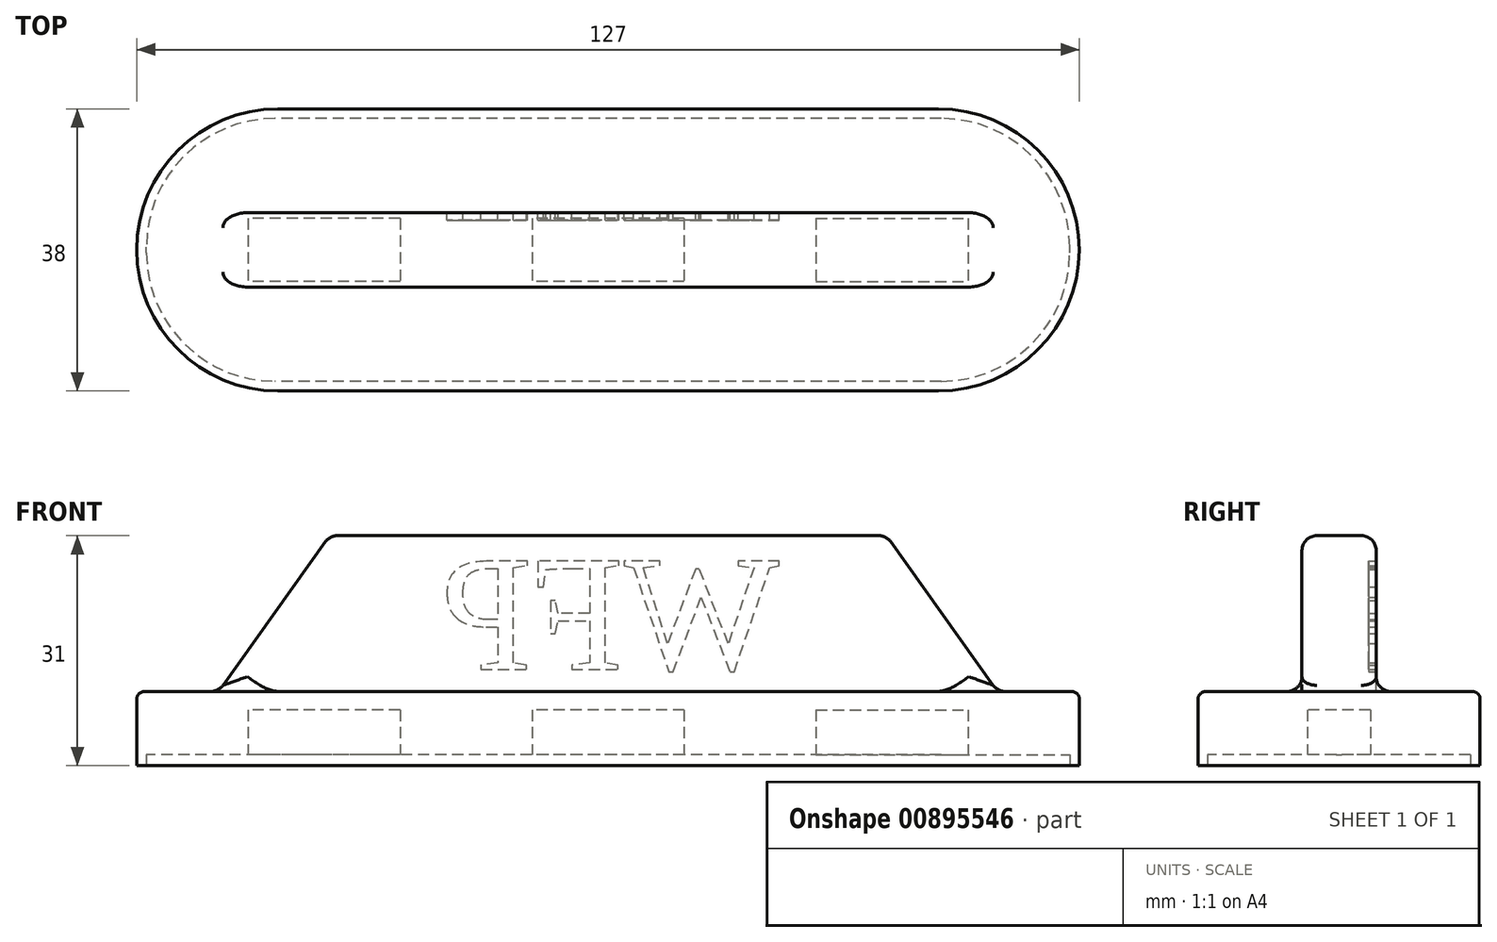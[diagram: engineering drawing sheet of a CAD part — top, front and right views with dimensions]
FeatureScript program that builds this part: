
annotation { "Feature Type Name" : "Feature", "Feature Type Description" : "" }
export const myFeature = defineFeature(function(context is Context, id is Id, definition is map)
    precondition{}
    {
        {
            var Q0;
            Q0=qCreatedBy(makeId("Top.planeOp"),FACE);
            var sketch = newSketch(context, id + "F0", { "sketchPlane" : qUnion([Q0])});
            skLineSegment(sketch, "E0.bottom", {"start": v(44.5, 19) * mm, "end": v(-44.5, 19) * mm});
            skLineSegment(sketch, "E0.top", {"start": v(44.5, -19) * mm, "end": v(-44.5, -19) * mm});
            skLineSegment(sketch, "E0.left", {"start": v(63.5, 0) * mm, "end": v(63.5, 0) * mm});
            skLineSegment(sketch, "E0.right", {"start": v(-63.5, 0) * mm, "end": v(-63.5, 0) * mm});
            skPoint(sketch, "E0.middle", {"position": v(0, 0) * mm});
            skPoint(sketch, "E1.visualSharp", {"position": v(-63.5, 19) * mm});
            skArc(sketch, "E1.filletArc", {"start": v(-44.5, 19) * mm, "mid": v(-57.94, 13.44) * mm, "end": v(-63.5, 0) * mm});
            skPoint(sketch, "E2.visualSharp", {"position": v(-63.5, -19) * mm});
            skArc(sketch, "E2.filletArc", {"start": v(-63.5, 0) * mm, "mid": v(-57.94, -13.44) * mm, "end": v(-44.5, -19) * mm});
            skPoint(sketch, "E3.visualSharp", {"position": v(63.5, 19) * mm});
            skArc(sketch, "E3.filletArc", {"start": v(63.5, 0) * mm, "mid": v(57.94, 13.44) * mm, "end": v(44.5, 19) * mm});
            skPoint(sketch, "E4.visualSharp", {"position": v(63.5, -19) * mm});
            skArc(sketch, "E4.filletArc", {"start": v(44.5, -19) * mm, "mid": v(57.94, -13.44) * mm, "end": v(63.5, 0) * mm});
            skSolve(sketch);
        }
        {
            var Q0;
            Q0=qSketchRegion(id+"F0",true);
            extrude(context, id + "F1", {"entities" : qUnion([Q0]), "depth" : 10 * mm, "offsetDistance" : 25 * mm});
        }
        {
            var Q0;
            Q0=makeQuery(id+"F1.opExtrude","CAP_FACE",FACE,{"disambiguationData":[OSD([sQuery(id+"F0.wireOp",EDGE,"E0.bottom"),sQuery(id+"F0.wireOp",EDGE,"E0.top"),sQuery(id+"F0.wireOp",EDGE,"E1.filletArc"),sQuery(id+"F0.wireOp",EDGE,"E2.filletArc"),sQuery(id+"F0.wireOp",EDGE,"E3.filletArc"),sQuery(id+"F0.wireOp",EDGE,"E4.filletArc")])],"isStart":false});
            var sketch = newSketch(context, id + "F2", { "sketchPlane" : qUnion([Q0])});
            skLineSegment(sketch, "E5.bottom", {"start": v(52.5, 5) * mm, "end": v(-52.5, 5) * mm});
            skLineSegment(sketch, "E5.top", {"start": v(52.5, -5) * mm, "end": v(-52.5, -5) * mm});
            skLineSegment(sketch, "E5.left", {"start": v(52.5, 5) * mm, "end": v(52.5, -5) * mm});
            skLineSegment(sketch, "E5.right", {"start": v(-52.5, 5) * mm, "end": v(-52.5, -5) * mm});
            skPoint(sketch, "E5.middle", {"position": v(0, 0) * mm});
            skSolve(sketch);
        }
        {
            var Q0;
            Q0=qSketchRegion(id+"F2",true);
            extrude(context, id + "F3", {"entities" : qUnion([Q0]), "operationType" : NewBodyOperationType.ADD, "depth" : 21 * mm, "offsetDistance" : 25 * mm});
        }
        {
            var Q0;
            Q0=makeQuery(id+"F3.opExtrude","SWEPT_FACE",FACE,{"disambiguationData":[OSD([sQuery(id+"F2.wireOp",EDGE,"E5.top")])]});
            var sketch = newSketch(context, id + "F4", { "sketchPlane" : qUnion([Q0])});
            skLineSegment(sketch, "E6", {"start": v(-52.5, 10) * mm, "end": v(-37.5, 31) * mm});
            skLineSegment(sketch, "E7", {"start": v(-37.5, 31) * mm, "end": v(-52.5, 31) * mm});
            skLineSegment(sketch, "E8", {"start": v(-52.5, 31) * mm, "end": v(-52.5, 10) * mm});
            skLineSegment(sketch, "E9", {"start": v(52.5, 10) * mm, "end": v(37.5, 31) * mm});
            skLineSegment(sketch, "E10", {"start": v(37.5, 31) * mm, "end": v(52.5, 31) * mm});
            skLineSegment(sketch, "E11", {"start": v(52.5, 31) * mm, "end": v(52.5, 10) * mm});
            skSolve(sketch);
        }
        {
            var Q0;
            Q0=makeQuery(id+"F4.imprint","IMPRINT",FACE,{"disambiguationData":[TD([[makeQuery(id+"F4.imprint","IMPRINT",EDGE,{"derivedFrom":sQuery(id+"F4.wireOp",EDGE,"E6")}),1.0]])]});
            var Q1;
            Q1=makeQuery(id+"F4.imprint","IMPRINT",FACE,{"disambiguationData":[TD([[makeQuery(id+"F4.imprint","IMPRINT",EDGE,{"derivedFrom":sQuery(id+"F4.wireOp",EDGE,"E9")}),-1.0]])]});
            extrude(context, id + "F5", {"entities" : qUnion([Q0, Q1]), "operationType" : NewBodyOperationType.REMOVE, "oppositeDirection" : true, "depth" : 10 * mm, "offsetDistance" : 25 * mm});
        }
        {
            var Q0;
            Q0=makeQuery(id+"F5.boolean.opBoolean","COPY",FACE,{"derivedFrom":makeQuery(id+"F5.opExtrude","SWEPT_FACE",FACE,{"disambiguationData":[OSD([sQuery(id+"F4.wireOp",EDGE,"E6")])]})});
            var Q1;
            Q1=makeQuery(id+"F3.opExtrude","CAP_FACE",FACE,{"disambiguationData":[OSD([sQuery(id+"F2.wireOp",EDGE,"E5.bottom"),sQuery(id+"F2.wireOp",EDGE,"E5.top"),sQuery(id+"F2.wireOp",EDGE,"E5.left"),sQuery(id+"F2.wireOp",EDGE,"E5.right")])],"isStart":false});
            var Q2;
            Q2=makeQuery(id+"F5.boolean.opBoolean","COPY",FACE,{"derivedFrom":makeQuery(id+"F5.opExtrude","SWEPT_FACE",FACE,{"disambiguationData":[OSD([sQuery(id+"F4.wireOp",EDGE,"E9")])]})});
            fillet(context, id + "F6", {"entities" : qUnion([Q0, Q1, Q2]), "radius" : 2 * mm, "tangentPropagation" : true, "allowEdgeOverflow" : false});
        }
        {
            var Q0;
            Q0=makeQuery(id+"F1.opExtrude","CAP_FACE",FACE,{"disambiguationData":[OSD([sQuery(id+"F0.wireOp",EDGE,"E0.bottom"),sQuery(id+"F0.wireOp",EDGE,"E0.top"),sQuery(id+"F0.wireOp",EDGE,"E1.filletArc"),sQuery(id+"F0.wireOp",EDGE,"E2.filletArc"),sQuery(id+"F0.wireOp",EDGE,"E3.filletArc"),sQuery(id+"F0.wireOp",EDGE,"E4.filletArc")])],"isStart":true});
            var sketch = newSketch(context, id + "F7", { "sketchPlane" : qUnion([Q0])});
            skPoint(sketch, "E12.middle", {"position": v(0, 0) * mm});
            skLineSegment(sketch, "E13.bottom", {"start": v(44.9, 17.7) * mm, "end": v(-44.9, 17.7) * mm});
            skLineSegment(sketch, "E13.top", {"start": v(44.9, -17.7) * mm, "end": v(-44.9, -17.7) * mm});
            skLineSegment(sketch, "E13.left", {"start": v(62.2, 0.4) * mm, "end": v(62.2, -0.4) * mm});
            skLineSegment(sketch, "E13.right", {"start": v(-62.2, 0.4) * mm, "end": v(-62.2, -0.4) * mm});
            skPoint(sketch, "E14.visualSharp", {"position": v(62.2, 17.7) * mm});
            skArc(sketch, "E14.filletArc", {"start": v(62.2, 0.4) * mm, "mid": v(57.13, 12.63) * mm, "end": v(44.9, 17.7) * mm});
            skPoint(sketch, "E15.visualSharp", {"position": v(62.2, -17.7) * mm});
            skArc(sketch, "E15.filletArc", {"start": v(44.9, -17.7) * mm, "mid": v(57.13, -12.63) * mm, "end": v(62.2, -0.4) * mm});
            skPoint(sketch, "E16.visualSharp", {"position": v(-62.2, -17.7) * mm});
            skArc(sketch, "E16.filletArc", {"start": v(-62.2, -0.4) * mm, "mid": v(-57.13, -12.63) * mm, "end": v(-44.9, -17.7) * mm});
            skPoint(sketch, "E17.visualSharp", {"position": v(-62.2, 17.7) * mm});
            skArc(sketch, "E17.filletArc", {"start": v(-44.9, 17.7) * mm, "mid": v(-57.13, 12.63) * mm, "end": v(-62.2, 0.4) * mm});
            skSolve(sketch);
        }
        {
            var Q0;
            Q0=makeQuery(id+"F7.imprint","IMPRINT",FACE,{"disambiguationData":[TD([[makeQuery(id+"F7.imprint","IMPRINT",EDGE,{"derivedFrom":sQuery(id+"F7.wireOp",EDGE,"E13.bottom")}),1.0]])]});
            extrude(context, id + "F8", {"entities" : qUnion([Q0]), "operationType" : NewBodyOperationType.REMOVE, "oppositeDirection" : true, "depth" : 1.5 * mm, "offsetDistance" : 25 * mm});
        }
        {
            var Q0;
            Q0=makeQuery(id+"F8.boolean.opBoolean","COPY",FACE,{"derivedFrom":makeQuery(id+"F8.opExtrude","CAP_FACE",FACE,{"disambiguationData":[OSD([sQuery(id+"F7.wireOp",EDGE,"E13.bottom"),sQuery(id+"F7.wireOp",EDGE,"E13.top"),sQuery(id+"F7.wireOp",EDGE,"E13.left"),sQuery(id+"F7.wireOp",EDGE,"E13.right"),sQuery(id+"F7.wireOp",EDGE,"E14.filletArc"),sQuery(id+"F7.wireOp",EDGE,"E15.filletArc"),sQuery(id+"F7.wireOp",EDGE,"E16.filletArc"),sQuery(id+"F7.wireOp",EDGE,"E17.filletArc")])],"isStart":false})});
            var sketch = newSketch(context, id + "F9", { "sketchPlane" : qUnion([Q0])});
            skLineSegment(sketch, "E18.bottom", {"start": v(10.25, -4.25) * mm, "end": v(-10.25, -4.25) * mm});
            skLineSegment(sketch, "E18.top", {"start": v(10.25, 4.25) * mm, "end": v(-10.25, 4.25) * mm});
            skLineSegment(sketch, "E18.left", {"start": v(10.25, -4.25) * mm, "end": v(10.25, 4.25) * mm});
            skLineSegment(sketch, "E18.right", {"start": v(-10.25, -4.25) * mm, "end": v(-10.25, 4.25) * mm});
            skPoint(sketch, "E18.middle", {"position": v(0, 0) * mm});
            skLineSegment(sketch, "E19.bottom", {"start": v(28, -4.25) * mm, "end": v(48.5, -4.25) * mm});
            skLineSegment(sketch, "E19.top", {"start": v(28, 4.25) * mm, "end": v(48.5, 4.25) * mm});
            skLineSegment(sketch, "E19.left", {"start": v(28, -4.25) * mm, "end": v(28, 4.25) * mm});
            skLineSegment(sketch, "E19.right", {"start": v(48.5, -4.25) * mm, "end": v(48.5, 4.25) * mm});
            skPoint(sketch, "E19.middle", {"position": v(38.25, 0) * mm});
            skLineSegment(sketch, "E20.bottom", {"start": v(-28, -4.25) * mm, "end": v(-48.5, -4.25) * mm});
            skLineSegment(sketch, "E20.top", {"start": v(-28, 4.25) * mm, "end": v(-48.5, 4.25) * mm});
            skLineSegment(sketch, "E20.left", {"start": v(-28, -4.25) * mm, "end": v(-28, 4.25) * mm});
            skLineSegment(sketch, "E20.right", {"start": v(-48.5, -4.25) * mm, "end": v(-48.5, 4.25) * mm});
            skPoint(sketch, "E20.middle", {"position": v(-38.25, 0) * mm});
            skSolve(sketch);
        }
        {
            var Q0;
            Q0=makeQuery(id+"F9.imprint","IMPRINT",FACE,{"disambiguationData":[TD([[makeQuery(id+"F9.imprint","IMPRINT",EDGE,{"derivedFrom":sQuery(id+"F9.wireOp",EDGE,"E19.bottom")}),1.0]])]});
            var Q1;
            Q1=makeQuery(id+"F9.imprint","IMPRINT",FACE,{"disambiguationData":[TD([[makeQuery(id+"F9.imprint","IMPRINT",EDGE,{"derivedFrom":sQuery(id+"F9.wireOp",EDGE,"E18.bottom")}),-1.0]])]});
            var Q2;
            Q2=makeQuery(id+"F9.imprint","IMPRINT",FACE,{"disambiguationData":[TD([[makeQuery(id+"F9.imprint","IMPRINT",EDGE,{"derivedFrom":sQuery(id+"F9.wireOp",EDGE,"E20.bottom")}),-1.0]])]});
            extrude(context, id + "F10", {"entities" : qUnion([Q0, Q1, Q2]), "operationType" : NewBodyOperationType.REMOVE, "oppositeDirection" : true, "depth" : 6 * mm, "offsetDistance" : 25 * mm});
        }
        {
            var Q0;
            Q0=makeQuery(id+"F1.opExtrude","CAP_EDGE",EDGE,{"disambiguationData":[OSD([sQuery(id+"F0.wireOp",EDGE,"E0.bottom")])],"isStart":false});
            fillet(context, id + "F11", {"entities" : qUnion([Q0]), "radius" : 1 * mm, "tangentPropagation" : true, "allowEdgeOverflow" : false});
        }
        {
            var Q0;
            Q0=makeQuery(id+"F3.opExtrude","SWEPT_FACE",FACE,{"disambiguationData":[OSD([sQuery(id+"F2.wireOp",EDGE,"E5.bottom")])]});
            var sketch = newSketch(context, id + "F12", { "sketchPlane" : qUnion([Q0])});
            skText(sketch, "E21", { "text": "WFP", "fontName": "Tinos-Regular.ttf"});
            const initialGuessF12  = {"E21": [-0.0231, 0.013, 1, 0, 0.016]};
            skSetInitialGuess(sketch, initialGuessF12);
            skSolve(sketch);
        }
        {
            var Q0;
            Q0=qSketchRegion(id+"F12",true);
            extrude(context, id + "F13", {"entities" : qUnion([Q0]), "operationType" : NewBodyOperationType.REMOVE, "oppositeDirection" : true, "depth" : 1 * mm, "offsetDistance" : 25 * mm});
        }
    });
